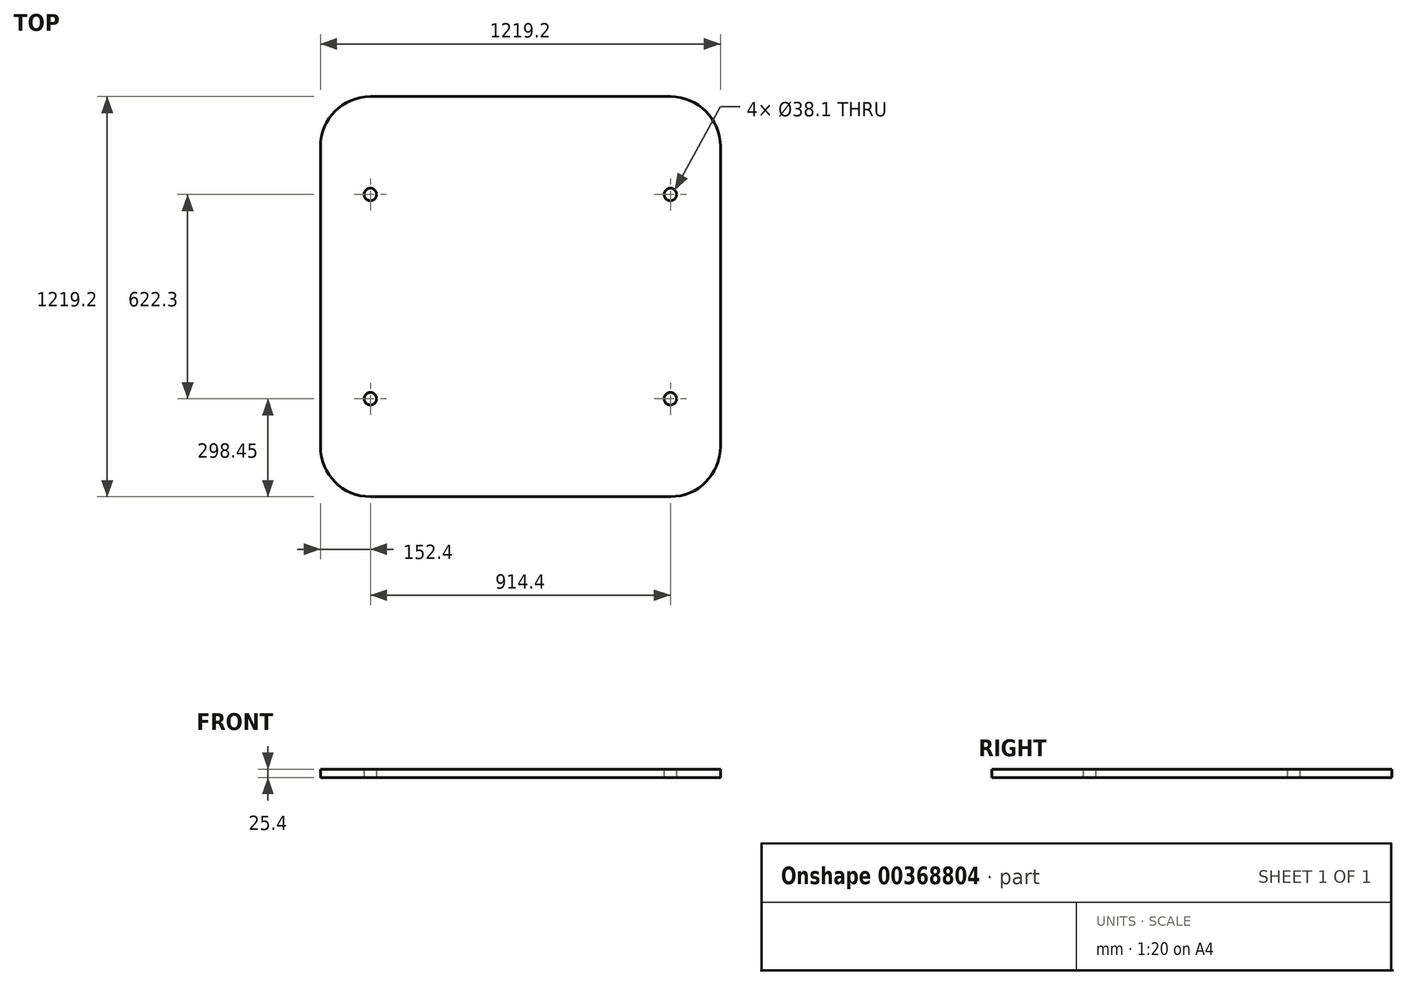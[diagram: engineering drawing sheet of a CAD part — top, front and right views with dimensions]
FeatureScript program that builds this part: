
annotation { "Feature Type Name" : "Feature", "Feature Type Description" : "" }
export const myFeature = defineFeature(function(context is Context, id is Id, definition is map)
    precondition{}
    {
        {
            var Q0;
            Q0=qCreatedBy(makeId("Top.planeOp"),FACE);
            var sketch = newSketch(context, id + "F0", { "sketchPlane" : qUnion([Q0])});
            skLineSegment(sketch, "E0.bottom", {"start": v(609.6, 609.6) * mm, "end": v(-609.6, 609.6) * mm});
            skLineSegment(sketch, "E0.top", {"start": v(609.6, -609.6) * mm, "end": v(-609.6, -609.6) * mm});
            skLineSegment(sketch, "E0.left", {"start": v(609.6, 609.6) * mm, "end": v(609.6, -609.6) * mm});
            skLineSegment(sketch, "E0.right", {"start": v(-609.6, 609.6) * mm, "end": v(-609.6, -609.6) * mm});
            skPoint(sketch, "E0.middle", {"position": v(0, 0) * mm});
            skSolve(sketch);
        }
        {
            var Q0;
            Q0=makeQuery(id+"F0.imprint","IMPRINT",FACE,{"disambiguationData":[TD([[makeQuery(id+"F0.imprint","IMPRINT",EDGE,{"derivedFrom":sQuery(id+"F0.wireOp",EDGE,"E0.bottom")}),1.0]])]});
            extrude(context, id + "F1", {"entities" : qUnion([Q0]), "depth" : 25.4 * mm});
        }
        {
            var Q0;
            Q0=makeQuery(id+"F1.opExtrude","SWEPT_EDGE",EDGE,{"disambiguationData":[OSD([sQuery(id+"F0.wireOp",EDGE,"E0.top"),sQuery(id+"F0.wireOp",EDGE,"E0.right")])]});
            var Q1;
            Q1=makeQuery(id+"F1.opExtrude","SWEPT_EDGE",EDGE,{"disambiguationData":[OSD([sQuery(id+"F0.wireOp",EDGE,"E0.top"),sQuery(id+"F0.wireOp",EDGE,"E0.left")])]});
            var Q2;
            Q2=makeQuery(id+"F1.opExtrude","SWEPT_EDGE",EDGE,{"disambiguationData":[OSD([sQuery(id+"F0.wireOp",EDGE,"E0.bottom"),sQuery(id+"F0.wireOp",EDGE,"E0.left")])]});
            var Q3;
            Q3=makeQuery(id+"F1.opExtrude","SWEPT_EDGE",EDGE,{"disambiguationData":[OSD([sQuery(id+"F0.wireOp",EDGE,"E0.bottom"),sQuery(id+"F0.wireOp",EDGE,"E0.right")])]});
            fillet(context, id + "F2", {"entities" : qUnion([Q0, Q1, Q2, Q3]), "radius" : 152.4 * mm, "tangentPropagation" : true, "allowEdgeOverflow" : false});
        }
        {
            var Q0;
            Q0=makeQuery(id+"F1.opExtrude","CAP_FACE",FACE,{"disambiguationData":[OSD([sQuery(id+"F0.wireOp",EDGE,"E0.bottom"),sQuery(id+"F0.wireOp",EDGE,"E0.top"),sQuery(id+"F0.wireOp",EDGE,"E0.left"),sQuery(id+"F0.wireOp",EDGE,"E0.right")])],"isStart":false});
            var sketch = newSketch(context, id + "F3", { "sketchPlane" : qUnion([Q0])});
            skLineSegment(sketch, "E1.bottom", {"start": v(457.2, 311.15) * mm, "end": v(-457.2, 311.15) * mm, "construction": true});
            skLineSegment(sketch, "E1.top", {"start": v(457.2, -311.15) * mm, "end": v(-457.2, -311.15) * mm, "construction": true});
            skLineSegment(sketch, "E1.left", {"start": v(457.2, 311.15) * mm, "end": v(457.2, -311.15) * mm, "construction": true});
            skLineSegment(sketch, "E1.right", {"start": v(-457.2, 311.15) * mm, "end": v(-457.2, -311.15) * mm, "construction": true});
            skPoint(sketch, "E1.middle", {"position": v(0, 0) * mm});
            skCircle(sketch, "E2", {"center": v(-457.2, 311.15) * mm, "radius": 19.05 * mm});
            skCircle(sketch, "E3", {"center": v(457.2, 311.15) * mm, "radius": 19.05 * mm});
            skCircle(sketch, "E4", {"center": v(457.2, -311.15) * mm, "radius": 19.05 * mm});
            skCircle(sketch, "E5", {"center": v(-457.2, -311.15) * mm, "radius": 19.05 * mm});
            skSolve(sketch);
        }
        {
            var Q0;
            Q0 = qSketchRegion(id + "F3", true);
            extrude(context, id + "F4", {"entities" : qUnion([Q0]), "operationType" : NewBodyOperationType.REMOVE, "oppositeDirection" : true, "depth" : 25.4 * mm});
        }
    });
